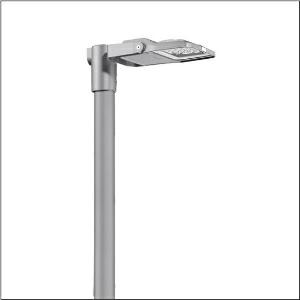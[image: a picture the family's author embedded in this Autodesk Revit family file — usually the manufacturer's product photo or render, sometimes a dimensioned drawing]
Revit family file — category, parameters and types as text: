
# Revit family: floodlight_fl_21_iq_micro___pl43_5xa7762a2a3a_62d6
name_source: partatom
category: Lighting Fixtures
units: mm (PartAtom-declared; Revit-internal decimal feet)

## family parameters
Cut with Voids When Loaded = No
Host = Face
Light Source = No
Part Type = Normal
Room Calculation Point = No
Round Connector Dimension = Use Diameter
Shared = No

## types (1)
- --- (1 x LED, 3040 lm, 23.1 W, 3000K)
    Apparent Load = 23 VA
    CIE Flux Codes = 29 80 99 100 100
    Color Rendering = 70
    Color Temperature = 3000K
    Default Elevation = 1800 mm
    Description = Floodlight FL 21 iQ micro, floodlight, primary light control with lens, of PMMA, primary optical cover: protective disc, of toughened safety glass, transparent, light distribution: PL43, light emission: direct distribution, installation type: surface-mounted, LED, High Power LED, rated luminous flux: 3.040lm, luminous efficacy: 132lm/W, light colour: 730, colour temperature: 3000K, control: Auto-Match, Temp-Guard, Night-Set, Smart-Wire, Desk-Remote (wireless, voltage-free reading and setting of iQ features in the workshop via application-optimized NFC function/RFID function), optimised constant luminous flux control (CLO 2.0), Street-Remote, with terminal, 6-pole, mains connection: 220..240V, AC, 50/60Hz, start of lifetime: 23W, end of service life: 24W, reduction: 11W, luminaire housing, of diecast aluminium, powder-coated, Siteco® metallic grey (DB 702S), corrosivity category C5 mid according to DIN EN ISO 12944, sealing non-destructively replaceable, please order mast flange separately, mast bracket, of steel, galvanised, powder-coated, Siteco® metallic grey (DB 702S), protection rating (complete): IP66, insulation class (complete): insulation class II (safety insulation), certification: CE, ENEC, VDE, protection symbol: D, impact resistance: IK07, permissible operating ambient temperature: -40..+40°C, permissible operating ambient temperature for outdoor applications: -40..+50°C, standard: DIN EN 12944, LABS conformity tested according to VDMA 24364:2018-05, packaging unit: 1 piece

Light Distribution: PL43
    Height = 65 mm
    Lamp = 1 x LED
    Lamp Light Flux = 3040 lm
    Lamp Power = 23.1 W
    Lamp count = 1
    Length = 312 mm
    Luminous efficacy = 132 lm/W
    Manufacturer = Siteco
    ModVariant = No
    Model = 5XA7762A2A3A
    Number of Poles = 1
    OnlyDefault = Yes
    Power Factor = 1
    Product Name = Floodlight FL 21 iQ micro | PL43
    Product group = floodlight | pylon annexe
    ProductGroupID = 6200
    Protection Class = Protection class II
    Protection Degree = IP 66
    RLX_Detail_Level = 1
    RLX_Emergency_Light_Flux = 0 lm
    RLX_Emergency_Type = 0
    RLX_Emergency_Type_DB = No
    RlxData = <blob elided: 101689 chars, md5=94c1dfab>
    Socket = socket
    Standby Power = 0 W
    System Light Flux = 3040 lm
    System Power = 23 W
    Type Comments = factory setting: luminous flux: 100 % | dim-lin: 254 | 455 mA
    Type Image = l_1007121.jpg
    URL = http://relux.com
    VarID = @adj_109949
    Voltage = 0 V
    Weight = 0.00 kg
    Width = 230 mm

## geometry (parser evidence)
native form markers: Blend x4, Sweep x13
no freeform markers — native parametric forms only
